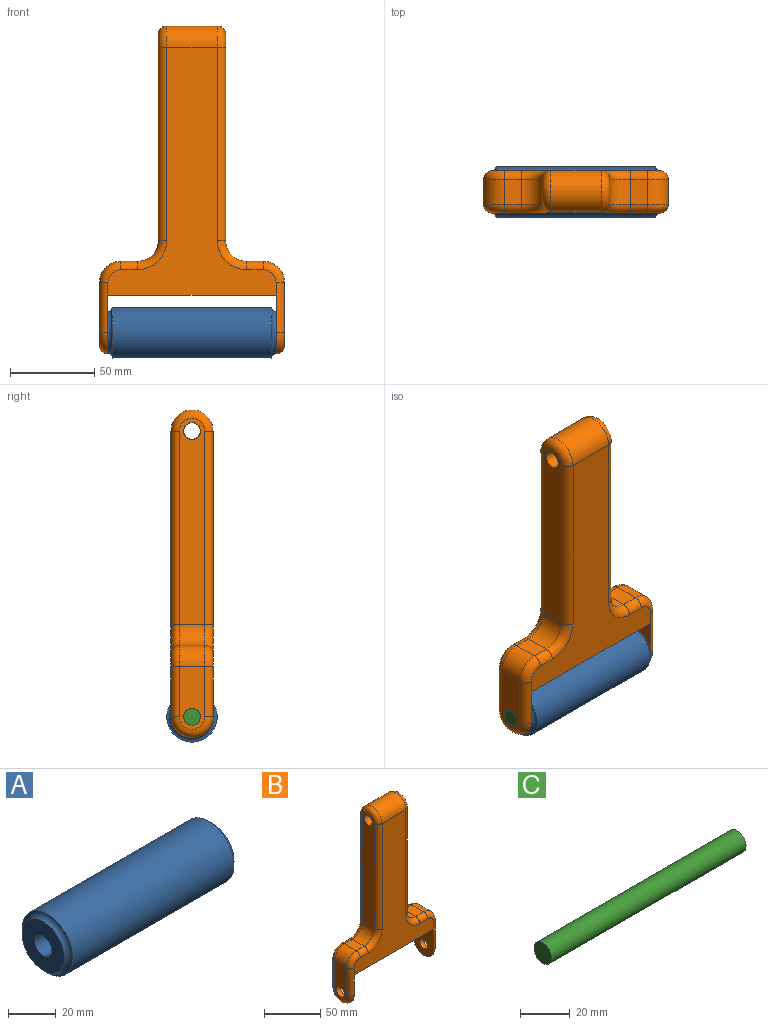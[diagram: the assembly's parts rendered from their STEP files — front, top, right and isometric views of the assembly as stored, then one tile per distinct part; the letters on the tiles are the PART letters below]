
ASSEMBLY  parts=3 mates=2
PART A: 6 faces, bbox 101.8x36.3x36.3 mm
  f0: plane 25x25mm, normal (1,0,0), area 412.3mm2, adj f1,f5
  f1: torus R=15mm, axis (-1,0,0), area 330.8mm2, adj f0,f2
  f2: cylinder r=15mm len=95mm, axis (-1,0,0), area 8953.5mm2, adj f1,f3
  f3: torus R=15mm, axis (-1,0,0), area 330.8mm2, adj f2,f4
  f4: plane 25x25mm, normal (-1,0,0), area 412.3mm2, adj f3,f5
  f5: cylinder r=5mm len=100mm, axis (1,0,0), area 3141.6mm2, adj f0,f4
PART B: 43 faces, bbox 112.1x27.1x197.1 mm
  f0: plane 122.5x15mm, normal (-1,0,0), area 1734.8mm2, adj f11,f28,f29,f31,f42
  f1: plane 15x10mm, normal (0,0,1), area 150mm2, adj f11,f14,f32,f35
  f2: plane 37.5x15mm, normal (-1,0,0), area 459.8mm2, adj f14,f36,f38,f39,f41
  f3: plane 35x25mm, normal (1,0,0), area 729.4mm2, adj f4,f36,f38,f39,f41
  f4: plane 100x25mm, normal (0,0,-1), area 2500mm2, adj f3,f5,f9,f10
  f5: plane 35x25mm, normal (-1,0,0), area 729.4mm2, adj f4,f24,f26,f27,f40
  f6: plane 37.5x15mm, normal (1,0,0), area 459.8mm2, adj f13,f24,f26,f27,f40
  f7: plane 15x10mm, normal (0,0,1), area 150mm2, adj f12,f13,f20,f23
  f8: plane 122.5x15mm, normal (1,0,0), area 1734.8mm2, adj f12,f16,f17,f19,f42
  f9: plane 147.5x100mm, normal (0,-1,0), area 5582.3mm2, adj f4,f15,f19,f21,f23,f25,f27,f31
  f10: plane 147.5x100mm, normal (0,1,0), area 5582.3mm2, adj f4,f15,f16,f18,f20,f22,f24,f28
  f11: cylinder r=12.5mm len=15mm, axis (0,1,0), area 294.5mm2, adj f0,f1,f30,f33
  f12: cylinder r=12.5mm len=15mm, axis (0,-1,0), area 294.5mm2, adj f7,f8,f18,f21
  f13: cylinder r=12.5mm len=15mm, axis (0,1,0), area 294.5mm2, adj f6,f7,f22,f25
  f14: cylinder r=12.5mm len=15mm, axis (0,-1,0), area 294.5mm2, adj f1,f2,f34,f37
  f15: cylinder r=12.5mm len=30mm, axis (1,0,0), area 1178.1mm2, adj f9,f10,f17,f29
  f16: cylinder r=5mm len=115mm, axis (0,0,1), area 903.2mm2, adj f8,f10,f17,f18
  f17: torus R=7.5mm, axis (1,0,0), area 263.6mm2, adj f8,f15,f16,f19
  f18: torus R=17.5mm, axis (0,-1,0), area 176.6mm2, adj f10,f12,f16,f20
  f19: cylinder r=5mm len=115mm, axis (0,0,-1), area 903.2mm2, adj f8,f9,f17,f21
  f20: cylinder r=5mm len=10mm, axis (-1,0,0), area 78.5mm2, adj f7,f10,f18,f22
  f21: torus R=17.5mm, axis (0,-1,0), area 176.6mm2, adj f9,f12,f19,f23
  f22: torus R=7.5mm, axis (0,-1,0), area 131.8mm2, adj f10,f13,f20,f24
  f23: cylinder r=5mm len=10mm, axis (1,0,0), area 78.5mm2, adj f7,f9,f21,f25
  f24: cylinder r=5mm len=30mm, axis (0,0,1), area 235.6mm2, adj f5,f6,f10,f22,f26
  f25: torus R=7.5mm, axis (0,-1,0), area 131.8mm2, adj f9,f13,f23,f27
  f26: torus R=7.5mm, axis (1,0,0), area 263.6mm2, adj f5,f6,f24,f27
  f27: cylinder r=5mm len=30mm, axis (0,0,-1), area 235.6mm2, adj f5,f6,f9,f25,f26
  f28: cylinder r=5mm len=115mm, axis (0,0,-1), area 903.2mm2, adj f0,f10,f29,f30
  f29: torus R=7.5mm, axis (1,0,0), area 263.6mm2, adj f0,f15,f28,f31
  f30: torus R=17.5mm, axis (0,-1,0), area 176.6mm2, adj f10,f11,f28,f32
  f31: cylinder r=5mm len=115mm, axis (0,0,1), area 903.2mm2, adj f0,f9,f29,f33
  f32: cylinder r=5mm len=10mm, axis (-1,0,0), area 78.5mm2, adj f1,f10,f30,f34
  f33: torus R=17.5mm, axis (0,-1,0), area 176.6mm2, adj f9,f11,f31,f35
  f34: torus R=7.5mm, axis (0,-1,0), area 131.8mm2, adj f10,f14,f32,f36
  f35: cylinder r=5mm len=10mm, axis (1,0,0), area 78.5mm2, adj f1,f9,f33,f37
  f36: cylinder r=5mm len=30mm, axis (0,0,-1), area 235.6mm2, adj f2,f3,f10,f34,f38
  f37: torus R=7.5mm, axis (0,-1,0), area 131.8mm2, adj f9,f14,f35,f39
  f38: torus R=7.5mm, axis (1,0,0), area 263.6mm2, adj f2,f3,f36,f39
  f39: cylinder r=5mm len=30mm, axis (0,0,1), area 235.6mm2, adj f2,f3,f9,f37,f38
  f40: cylinder r=5mm len=10mm, axis (1,0,0), area 157.1mm2, adj f5,f6
  f41: cylinder r=5mm len=10mm, axis (1,0,0), area 157.1mm2, adj f2,f3
  f42: cylinder r=5mm len=40mm, axis (-1,0,0), area 1256.6mm2, adj f0,f8
PART C: 3 faces, bbox 110x10x10 mm
  f0: cylinder r=5mm len=110mm, axis (-1,0,0), area 3455.8mm2, adj f1,f2
  f1: plane 10x10mm, normal (1,0,0), area 78.5mm2, adj f0
  f2: plane 10x10mm, normal (-1,0,0), area 78.5mm2, adj f0
PLACE A t=(-30,-12.5,-167.5)mm
PLACE B at identity fixed
PLACE C t=(-35,-12.5,-182.5)mm
MATE revolute A.f1 <-> C.f0  axis (1,0,0) through (70,-12.5,-182.5)mm
MATE revolute C.f0 <-> B.f26  axis (-1,0,0) through (75,-12.5,-182.5)mm
